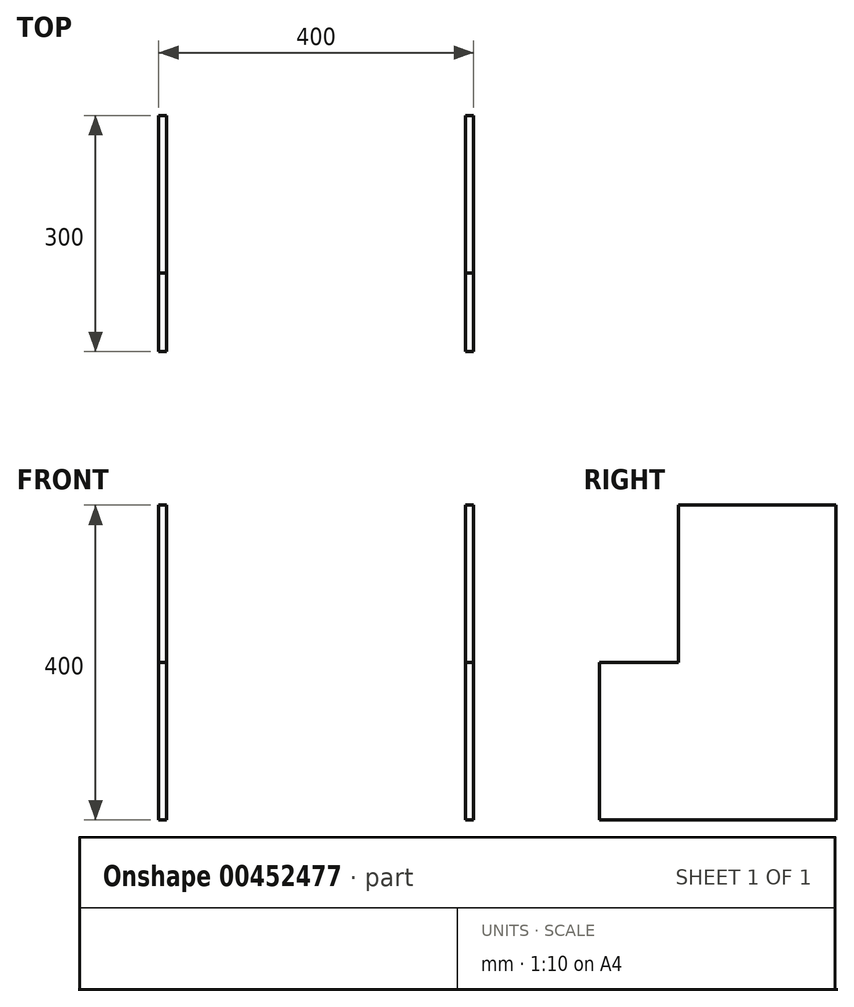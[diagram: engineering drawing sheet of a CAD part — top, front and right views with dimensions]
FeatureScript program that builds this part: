
annotation { "Feature Type Name" : "Feature", "Feature Type Description" : "" }
export const myFeature = defineFeature(function(context is Context, id is Id, definition is map)
    precondition{}
    {
        {
            var Q0;
            Q0=qCreatedBy(makeId("Right.planeOp"),FACE);
            var sketch = newSketch(context, id + "F0", { "sketchPlane" : qUnion([Q0])});
            skLineSegment(sketch, "E0.bottom", {"start": v(0, 0) * mm, "end": v(300, 0) * mm});
            skLineSegment(sketch, "E0.top", {"start": v(0, 400) * mm, "end": v(300, 400) * mm});
            skLineSegment(sketch, "E0.left", {"start": v(0, 0) * mm, "end": v(0, 400) * mm});
            skLineSegment(sketch, "E0.right", {"start": v(300, 0) * mm, "end": v(300, 400) * mm});
            skSolve(sketch);
        }
        {
            var Q0;
            Q0=makeQuery(id+"F0.imprint","IMPRINT",FACE,{"disambiguationData":[TD([[makeQuery(id+"F0.imprint","IMPRINT",EDGE,{"derivedFrom":sQuery(id+"F0.wireOp",EDGE,"E0.bottom")}),1.0]])]});
            var sketch = newSketch(context, id + "F1", { "sketchPlane" : qUnion([Q0])});
            skSolve(sketch);
        }
        {
            var Q0;
            Q0 = qSketchRegion(id + "F1", true);
            var Q1;
            Q1=makeQuery(id+"F0.imprint","IMPRINT",FACE,{"disambiguationData":[TD([[makeQuery(id+"F0.imprint","IMPRINT",EDGE,{"derivedFrom":sQuery(id+"F0.wireOp",EDGE,"E0.bottom")}),1.0]])]});
            extrude(context, id + "F2", {"entities" : qUnion([Q0, Q1]), "depth" : 10 * mm});
        }
        {
            var Q0;
            Q0=makeQuery(id+"F1.imprint","IMPRINT",FACE,{"disambiguationData":[TD([[makeQuery(id+"F1.imprint","IMPRINT",EDGE,{"derivedFrom":makeQuery(id+"F0.imprint","IMPRINT",EDGE,{"derivedFrom":sQuery(id+"F0.wireOp",EDGE,"E0.bottom")})}),1.0]])]});
            cPlane(context, id + "F3", {"entities" : qUnion([Q0]), "cplaneType" : CPlaneType.OFFSET, "offset" : 200 * mm, "width" : 150 * mm, "height" : 150 * mm});
        }
        {
            var Q0;
            Q0=makeQuery(id+"F2.opExtrude","SWEPT_BODY",BODY,{"disambiguationData":[OSD([sQuery(id+"F0.wireOp",EDGE,"E0.bottom"),sQuery(id+"F0.wireOp",EDGE,"E0.top"),sQuery(id+"F0.wireOp",EDGE,"E0.left"),sQuery(id+"F0.wireOp",EDGE,"E0.right")])]});
            var Q1;
            Q1=qCreatedBy(id+"F3.planeOp",FACE);
            mirror(context, id + "F4", {"entities" : qUnion([Q0]), "mirrorPlane" : qUnion([Q1])});
        }
        {
            var Q0;
            Q0=makeQuery(id+"F4.opPattern","COPY",FACE,{"derivedFrom":makeQuery(id+"F2.opExtrude","CAP_FACE",FACE,{"disambiguationData":[OSD([sQuery(id+"F0.wireOp",EDGE,"E0.bottom"),sQuery(id+"F0.wireOp",EDGE,"E0.top"),sQuery(id+"F0.wireOp",EDGE,"E0.left"),sQuery(id+"F0.wireOp",EDGE,"E0.right")])],"isStart":true}),"instanceName":"1"});
            var sketch = newSketch(context, id + "F5", { "sketchPlane" : qUnion([Q0])});
            skLineSegment(sketch, "E1.bottom", {"start": v(100, 400) * mm, "end": v(0, 400) * mm});
            skLineSegment(sketch, "E1.top", {"start": v(100, 200) * mm, "end": v(0, 200) * mm});
            skLineSegment(sketch, "E1.left", {"start": v(100, 400) * mm, "end": v(100, 200) * mm});
            skLineSegment(sketch, "E1.right", {"start": v(0, 400) * mm, "end": v(0, 200) * mm});
            skSolve(sketch);
        }
        {
            var Q0;
            Q0=makeQuery(id+"F5.imprint","IMPRINT",FACE,{"disambiguationData":[TD([[makeQuery(id+"F5.imprint","IMPRINT",EDGE,{"derivedFrom":sQuery(id+"F5.wireOp",EDGE,"E1.bottom")}),-1.0]])]});
            extrude(context, id + "F6", {"entities" : qUnion([Q0]), "operationType" : NewBodyOperationType.REMOVE, "endBound" : BoundingType.THROUGH_ALL, "oppositeDirection" : true, "depth" : 25 * mm});
        }
    });
